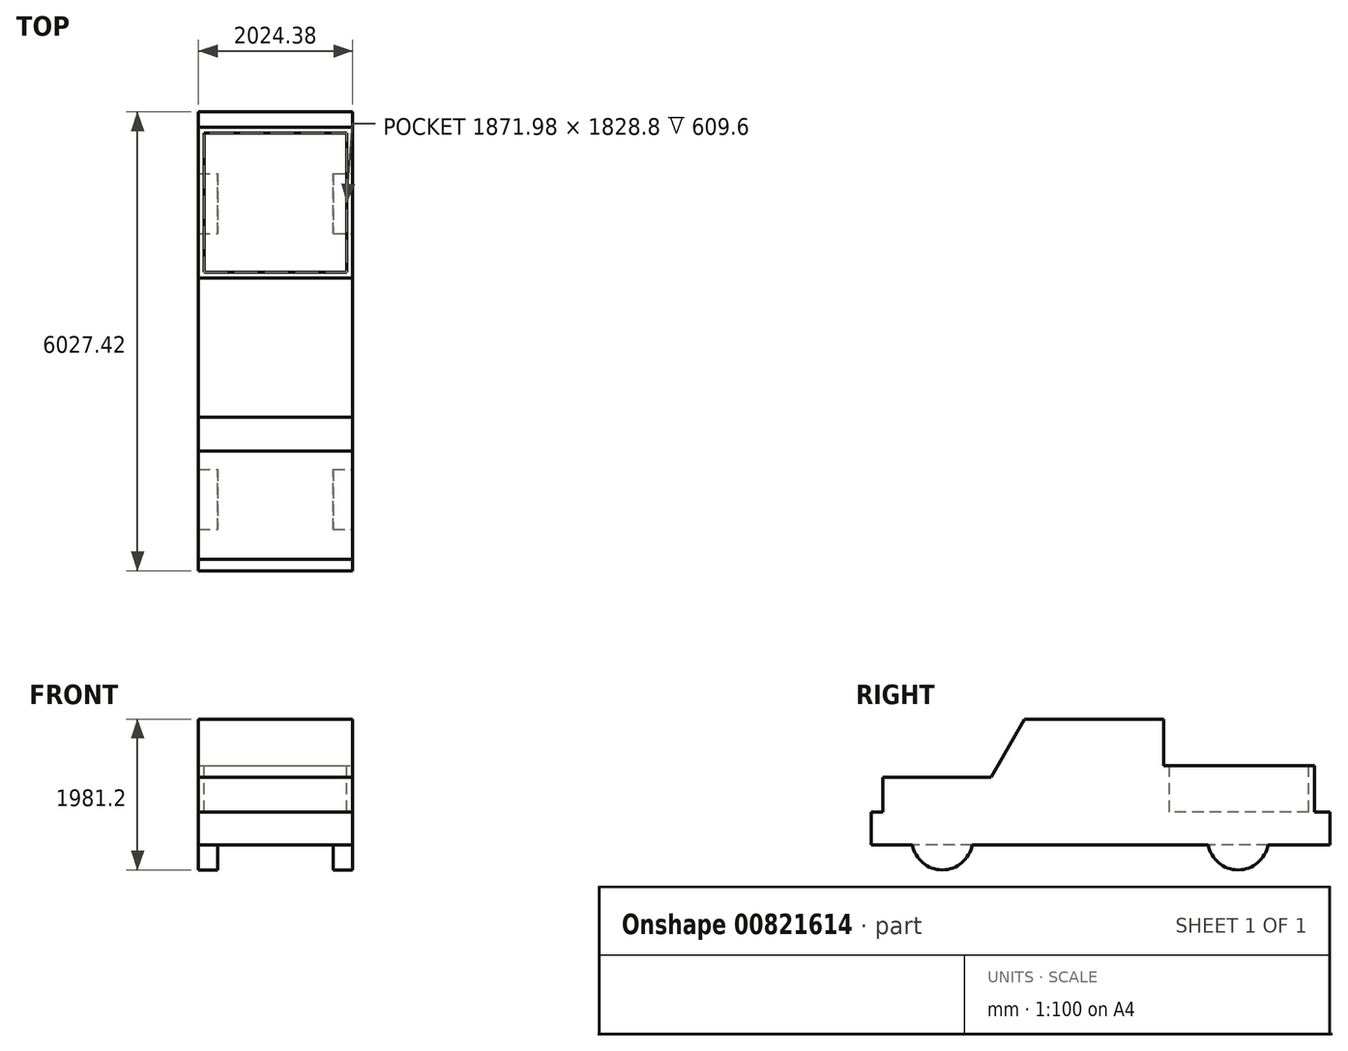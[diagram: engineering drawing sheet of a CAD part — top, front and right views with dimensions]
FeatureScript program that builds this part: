
annotation { "Feature Type Name" : "Feature", "Feature Type Description" : "" }
export const myFeature = defineFeature(function(context is Context, id is Id, definition is map)
    precondition{}
    {
        {
            var Q0;
            Q0=qCreatedBy(makeId("Top.planeOp"),FACE);
            var sketch = newSketch(context, id + "F0", { "sketchPlane" : qUnion([Q0])});
            skLineSegment(sketch, "E0.bottom", {"start": v(0, 0) * mm, "end": v(2024.38, 0) * mm});
            skLineSegment(sketch, "E0.top", {"start": v(0, 6027.42) * mm, "end": v(2024.38, 6027.42) * mm});
            skLineSegment(sketch, "E0.left", {"start": v(0, 0) * mm, "end": v(0, 6027.42) * mm});
            skLineSegment(sketch, "E0.right", {"start": v(2024.38, 0) * mm, "end": v(2024.38, 6027.42) * mm});
            skSolve(sketch);
        }
        {
            var Q0;
            Q0 = qSketchRegion(id + "F0", true);
            extrude(context, id + "F1", {"entities" : qUnion([Q0]), "depth" : 1981.2 * mm, "offsetDistance" : 25.4 * mm});
        }
        {
            var Q0;
            Q0=makeQuery(id+"F1.opExtrude","SWEPT_FACE",FACE,{"disambiguationData":[OSD([sQuery(id+"F0.wireOp",EDGE,"E0.right")])]});
            var sketch = newSketch(context, id + "F2", { "sketchPlane" : qUnion([Q0])});
            skLineSegment(sketch, "E1", {"start": v(6027.42, 762) * mm, "end": v(5824.22, 762) * mm});
            skLineSegment(sketch, "E2", {"start": v(5824.22, 762) * mm, "end": v(5824.22, 1371.6) * mm});
            skLineSegment(sketch, "E3", {"start": v(5824.22, 1371.6) * mm, "end": v(3843.02, 1371.6) * mm});
            skLineSegment(sketch, "E4", {"start": v(3843.02, 1371.6) * mm, "end": v(3843.02, 1981.2) * mm});
            skLineSegment(sketch, "E5", {"start": v(3843.02, 1981.2) * mm, "end": v(6027.42, 1981.2) * mm});
            skLineSegment(sketch, "E6", {"start": v(6027.42, 1981.2) * mm, "end": v(6027.42, 762) * mm});
            skLineSegment(sketch, "E7", {"start": v(2014.22, 1981.2) * mm, "end": v(1574.28, 1219.2) * mm});
            skLineSegment(sketch, "E8", {"start": v(1574.28, 1219.2) * mm, "end": v(152.4, 1219.2) * mm});
            skLineSegment(sketch, "E9", {"start": v(152.4, 1219.2) * mm, "end": v(152.4, 762) * mm});
            skLineSegment(sketch, "E10", {"start": v(152.4, 762) * mm, "end": v(0, 762) * mm});
            skLineSegment(sketch, "E11", {"start": v(0, 762) * mm, "end": v(0, 1981.2) * mm});
            skLineSegment(sketch, "E12", {"start": v(0, 1981.2) * mm, "end": v(2014.22, 1981.2) * mm});
            skSolve(sketch);
        }
        {
            var Q0;
            Q0 = qSketchRegion(id + "F2", true);
            extrude(context, id + "F3", {"entities" : qUnion([Q0]), "operationType" : NewBodyOperationType.REMOVE, "endBound" : BoundingType.THROUGH_ALL, "oppositeDirection" : true, "depth" : 25.4 * mm, "offsetDistance" : 25.4 * mm});
        }
        {
            var Q0;
            Q0=makeQuery(id+"F1.opExtrude","SWEPT_FACE",FACE,{"disambiguationData":[OSD([sQuery(id+"F0.wireOp",EDGE,"E0.bottom")])]});
            var sketch = newSketch(context, id + "F4", { "sketchPlane" : qUnion([Q0])});
            skLineSegment(sketch, "E13.bottom", {"start": v(254, 0) * mm, "end": v(1770.38, 0) * mm});
            skLineSegment(sketch, "E13.top", {"start": v(254, 330.2) * mm, "end": v(1770.38, 330.2) * mm});
            skLineSegment(sketch, "E13.left", {"start": v(254, 0) * mm, "end": v(254, 330.2) * mm});
            skLineSegment(sketch, "E13.right", {"start": v(1770.38, 0) * mm, "end": v(1770.38, 330.2) * mm});
            skSolve(sketch);
        }
        {
            var Q0;
            Q0 = qSketchRegion(id + "F4", true);
            extrude(context, id + "F5", {"entities" : qUnion([Q0]), "operationType" : NewBodyOperationType.REMOVE, "endBound" : BoundingType.THROUGH_ALL, "oppositeDirection" : true, "depth" : 25.4 * mm, "offsetDistance" : 25.4 * mm});
        }
        {
            var Q0;
            Q0=makeQuery(id+"F1.opExtrude","SWEPT_FACE",FACE,{"disambiguationData":[OSD([sQuery(id+"F0.wireOp",EDGE,"E0.right")])]});
            var sketch = newSketch(context, id + "F6", { "sketchPlane" : qUnion([Q0])});
            skLineSegment(sketch, "E14", {"start": v(0, 330.2) * mm, "end": v(540.61, 330.2) * mm});
            skLineSegment(sketch, "E15", {"start": v(1328.42, 330.2) * mm, "end": v(4426.81, 330.2) * mm});
            skLineSegment(sketch, "E16", {"start": v(5214.62, 330.2) * mm, "end": v(6027.42, 330.2) * mm});
            skLineSegment(sketch, "E17", {"start": v(6027.42, 330.2) * mm, "end": v(6027.42, 0) * mm});
            skLineSegment(sketch, "E18", {"start": v(6027.42, 0) * mm, "end": v(0, 0) * mm});
            skLineSegment(sketch, "E19", {"start": v(0, 0) * mm, "end": v(0, 330.2) * mm});
            skArc(sketch, "E20", {"start": v(540.61, 330.2) * mm, "mid": v(934.52, 0) * mm, "end": v(1328.42, 330.2) * mm});
            skArc(sketch, "E21", {"start": v(4426.81, 330.2) * mm, "mid": v(4820.72, 0) * mm, "end": v(5214.62, 330.2) * mm});
            skSolve(sketch);
        }
        {
            var Q0;
            Q0 = qSketchRegion(id + "F6", true);
            extrude(context, id + "F7", {"entities" : qUnion([Q0]), "operationType" : NewBodyOperationType.REMOVE, "endBound" : BoundingType.THROUGH_ALL, "oppositeDirection" : true, "depth" : 25.4 * mm, "offsetDistance" : 25.4 * mm});
        }
        {
            var Q0;
            Q0=makeQuery(id+"F3.boolean.opBoolean","COPY",FACE,{"derivedFrom":makeQuery(id+"F3.opExtrude","SWEPT_FACE",FACE,{"disambiguationData":[OSD([sQuery(id+"F2.wireOp",EDGE,"E3")])]})});
            var sketch = newSketch(context, id + "F8", { "sketchPlane" : qUnion([Q0])});
            skLineSegment(sketch, "E22.0", {"start": v(76.2, 3919.22) * mm, "end": v(76.2, 5748.02) * mm});
            skLineSegment(sketch, "E22.1", {"start": v(76.2, 3919.22) * mm, "end": v(1948.18, 3919.22) * mm});
            skLineSegment(sketch, "E22.2", {"start": v(1948.18, 5748.02) * mm, "end": v(1948.18, 3919.22) * mm});
            skLineSegment(sketch, "E22.3", {"start": v(76.2, 5748.02) * mm, "end": v(1948.18, 5748.02) * mm});
            skSolve(sketch);
        }
        {
            var Q0;
            Q0 = qSketchRegion(id + "F8", true);
            var Q1;
            Q1=makeQuery(id+"F3.boolean.opBoolean","COPY",FACE,{"derivedFrom":makeQuery(id+"F3.opExtrude","SWEPT_FACE",FACE,{"disambiguationData":[OSD([sQuery(id+"F2.wireOp",EDGE,"E1")])]})});
            extrude(context, id + "F9", {"entities" : qUnion([Q0]), "operationType" : NewBodyOperationType.REMOVE, "endBound" : BoundingType.UP_TO_SURFACE, "oppositeDirection" : true, "depth" : 25.4 * mm, "endBoundEntityFace" : qUnion([Q1]), "offsetDistance" : 25.4 * mm});
        }
    });
